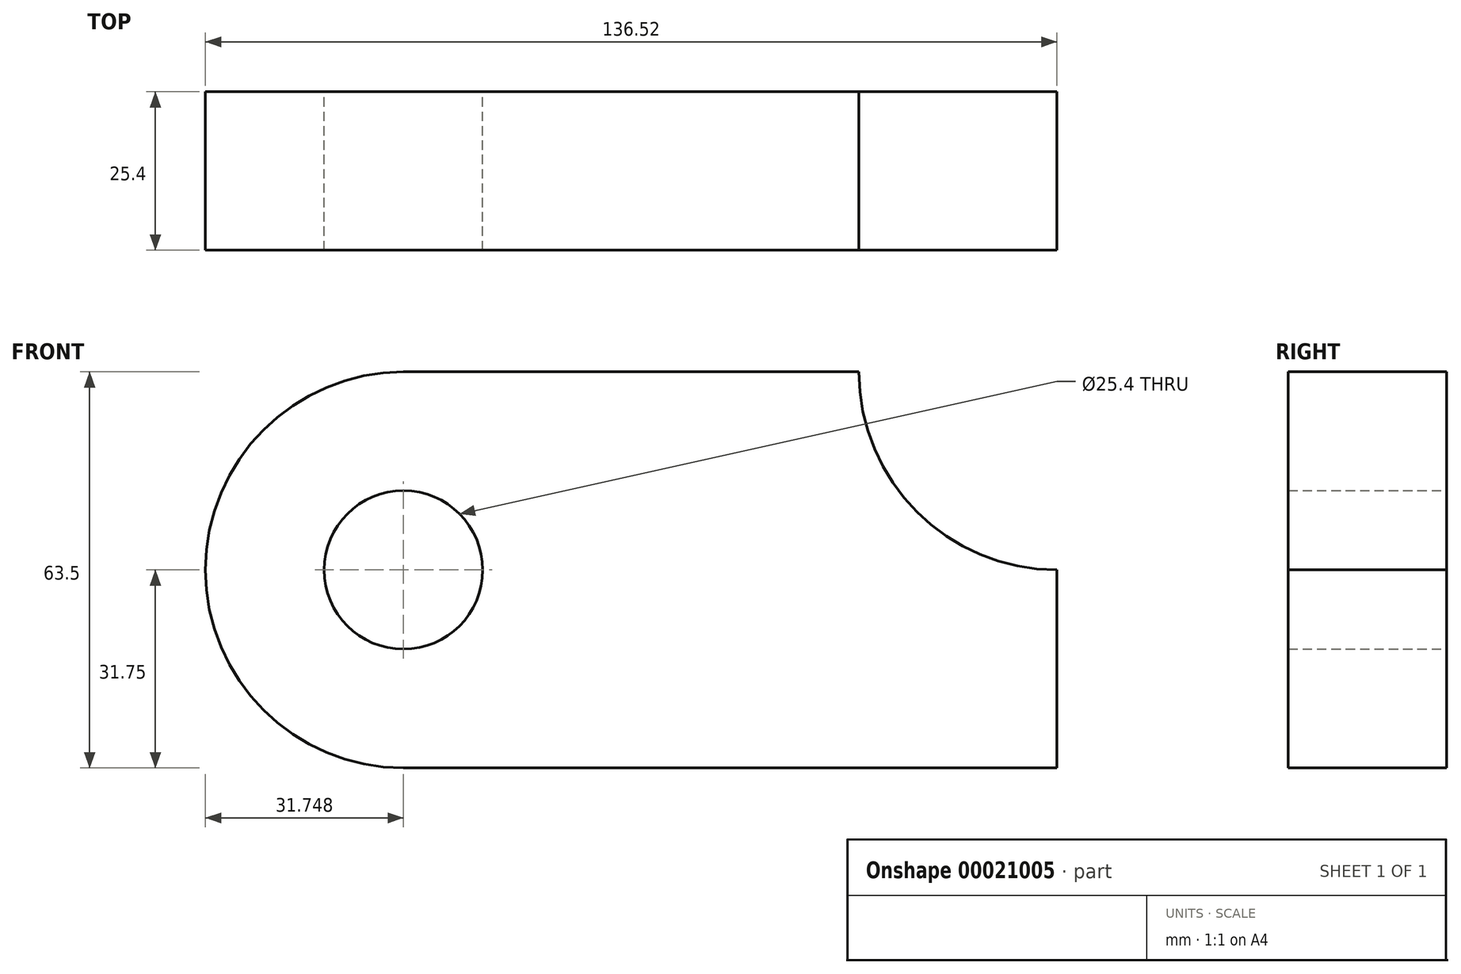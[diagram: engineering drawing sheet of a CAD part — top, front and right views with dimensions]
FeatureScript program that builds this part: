
annotation { "Feature Type Name" : "Feature", "Feature Type Description" : "" }
export const myFeature = defineFeature(function(context is Context, id is Id, definition is map)
    precondition{}
    {
        {
            var Q0;
            Q0=qCreatedBy(makeId("Front.planeOp"),FACE);
            var sketch = newSketch(context, id + "F0", { "sketchPlane" : qUnion([Q0])});
            skLineSegment(sketch, "E0.rect.bottom", {"start": v(-100.38, -31.75) * mm, "end": v(4.4, -31.75) * mm});
            skLineSegment(sketch, "E0.rect.top", {"start": v(-100.38, 31.75) * mm, "end": v(-27.36, 31.75) * mm});
            skLineSegment(sketch, "E0.rect.right", {"start": v(4.4, -31.75) * mm, "end": v(4.4, 0) * mm});
            skPoint(sketch, "E0.rect.middle", {"position": v(-48, 0) * mm});
            skArc(sketch, "E1", {"start": v(-100.38, 31.75) * mm, "mid": v(-132.13, 0) * mm, "end": v(-100.38, -31.75) * mm});
            skCircle(sketch, "E2", {"center": v(-100.38, 0) * mm, "radius": 12.7 * mm});
            skArc(sketch, "E3", {"start": v(-27.36, 31.75) * mm, "mid": v(-18.06, 9.3) * mm, "end": v(4.4, 0) * mm});
            skSolve(sketch);
        }
        {
            var Q0;
            {var subQ8=sQuery(id+"F0.wireOp",EDGE,"E0.rect.bottom");Q0=makeQuery(id+"F0.imprint","IMPRINT",FACE,{"disambiguationData":[TD([[makeQuery(id+"F0.imprint","IMPRINT",EDGE,{"derivedFrom":subQ8}),1.0]])]});}
            var Q1;
            {var subQ0=sQuery(id+"F0.wireOp",EDGE,"E2");var subQ1=sQuery(id+"F0.wireOp",EDGE,"E0.rect.left");var subQ3=makeQuery(id+"F0.imprint","INTERSECT",VERTEX,{"disambiguationData":[OD(0.0)],"derivedFrom":[subQ1,subQ0]});Q1=makeQuery(id+"F0.imprint","IMPRINT",FACE,{"disambiguationData":[TD([[makeQuery(id+"F0.imprint","IMPRINT",EDGE,{"disambiguationData":[TD([[subQ3,1.0]])],"derivedFrom":subQ0}),-1.0]])]});}
            var Q2;
            {var subQ0=sQuery(id+"F0.wireOp",EDGE,"E2");var subQ1=sQuery(id+"F0.wireOp",EDGE,"E0.rect.left");var subQ3=makeQuery(id+"F0.imprint","INTERSECT",VERTEX,{"disambiguationData":[OD(0.0)],"derivedFrom":[subQ1,subQ0]});Q2=makeQuery(id+"F0.imprint","IMPRINT",FACE,{"disambiguationData":[TD([[makeQuery(id+"F0.imprint","IMPRINT",EDGE,{"disambiguationData":[TD([[subQ3,-1.0]])],"derivedFrom":subQ0}),-1.0]])]});}
            extrude(context, id + "F1", {"entities" : qUnion([Q0, Q1, Q2]), "depth" : 25.4 * mm});
        }
    });
